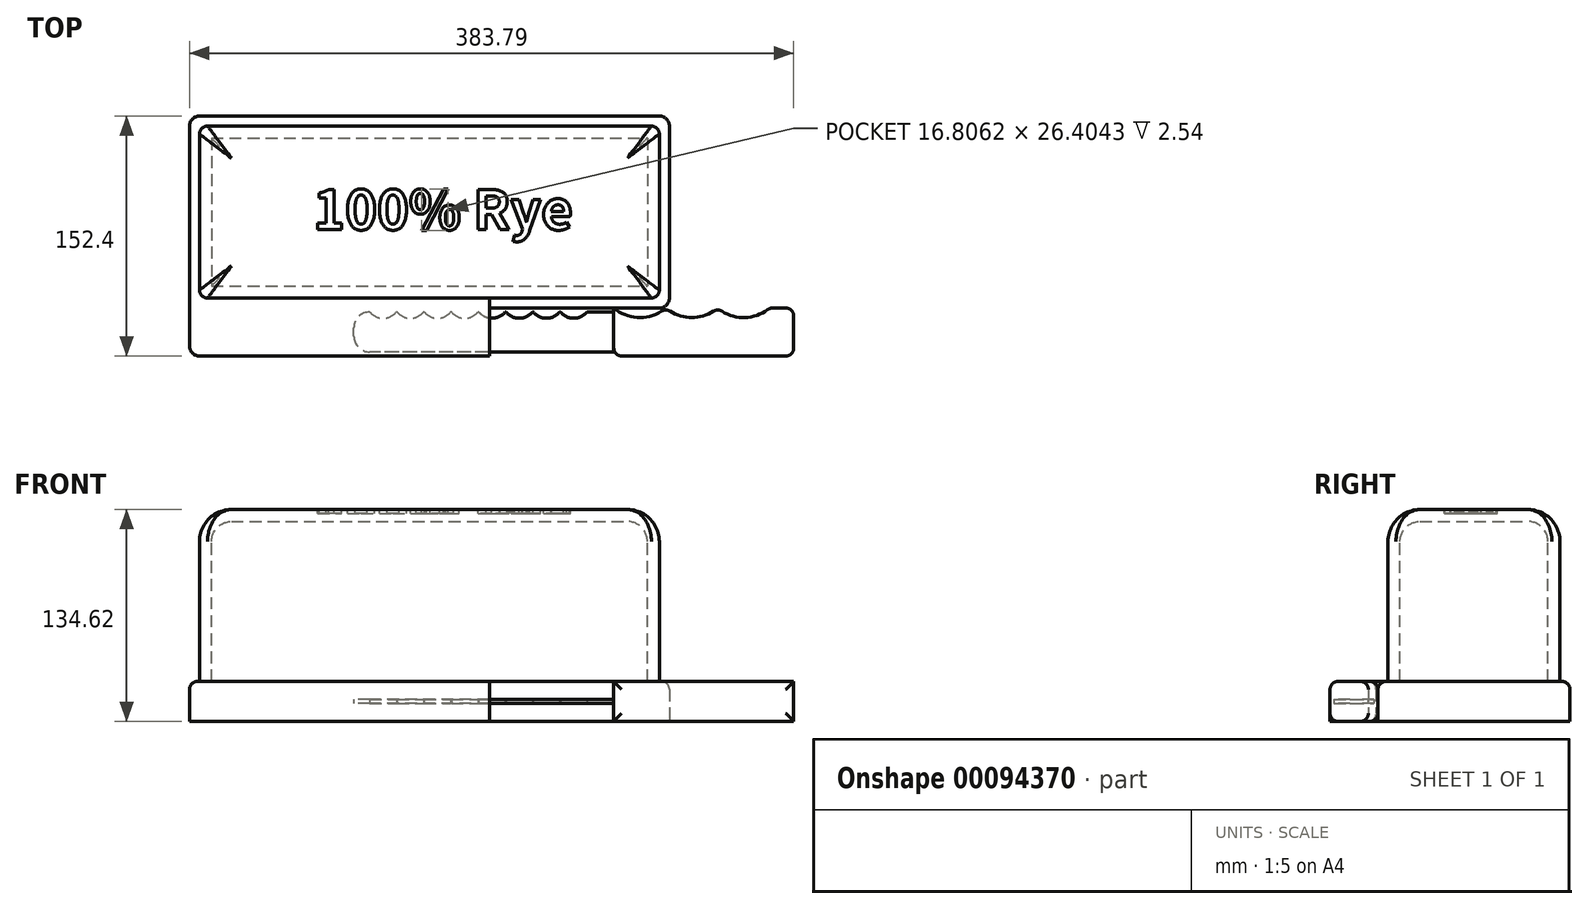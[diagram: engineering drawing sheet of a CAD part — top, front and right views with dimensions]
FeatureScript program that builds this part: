
annotation { "Feature Type Name" : "Feature", "Feature Type Description" : "" }
export const myFeature = defineFeature(function(context is Context, id is Id, definition is map)
    precondition{}
    {
        {
            var Q0;
            Q0=qCreatedBy(makeId("Top.planeOp"),FACE);
            var sketch = newSketch(context, id + "F0", { "sketchPlane" : qUnion([Q0])});
            skLineSegment(sketch, "E0.bottom", {"start": v(-146.05, 76.2) * mm, "end": v(146.05, 76.2) * mm});
            skLineSegment(sketch, "E0.top", {"start": v(-146.05, -76.2) * mm, "end": v(152.4, -76.2) * mm});
            skLineSegment(sketch, "E0.left", {"start": v(-152.4, 69.85) * mm, "end": v(-152.4, -69.85) * mm});
            skLineSegment(sketch, "E0.right", {"start": v(152.4, 69.85) * mm, "end": v(152.4, -45.72) * mm});
            skPoint(sketch, "E0.middle", {"position": v(0, 0) * mm});
            skPoint(sketch, "E1.visualSharp", {"position": v(-152.4, 76.2) * mm});
            skArc(sketch, "E1.filletArc", {"start": v(-146.05, 76.2) * mm, "mid": v(-150.54, 74.34) * mm, "end": v(-152.4, 69.85) * mm});
            skPoint(sketch, "E2.visualSharp", {"position": v(152.4, 76.2) * mm});
            skArc(sketch, "E2.filletArc", {"start": v(152.4, 69.85) * mm, "mid": v(150.54, 74.34) * mm, "end": v(146.05, 76.2) * mm});
            skLineSegment(sketch, "E3.top", {"start": v(152.4, -45.72) * mm, "end": v(38.1, -45.72) * mm});
            skLineSegment(sketch, "E3.left", {"start": v(152.4, -76.2) * mm, "end": v(152.4, -45.72) * mm});
            skLineSegment(sketch, "E3.right", {"start": v(38.1, -76.2) * mm, "end": v(38.1, -45.72) * mm});
            skLineSegment(sketch, "E4", {"start": v(152.4, -45.72) * mm, "end": v(152.4, -76.2) * mm});
            skArc(sketch, "E5", {"start": v(38.1, -45.72) * mm, "mid": v(54.61, -51.82) * mm, "end": v(71.12, -45.72) * mm});
            skArc(sketch, "E6", {"start": v(71.12, -45.72) * mm, "mid": v(87.63, -51.82) * mm, "end": v(104.14, -45.72) * mm});
            skArc(sketch, "E7", {"start": v(104.14, -45.72) * mm, "mid": v(120.65, -51.82) * mm, "end": v(137.16, -45.72) * mm});
            skPoint(sketch, "E8.visualSharp", {"position": v(-152.4, -76.2) * mm});
            skArc(sketch, "E8.filletArc", {"start": v(-152.4, -69.85) * mm, "mid": v(-150.54, -74.34) * mm, "end": v(-146.05, -76.2) * mm});
            skSolve(sketch);
        }
        {
            var Q0;
            {var subQ1=sQuery(id+"F0.wireOp",EDGE,"E3.right");Q0=makeQuery(id+"F0.imprint","IMPRINT",FACE,{"disambiguationData":[TD([[makeQuery(id+"F0.imprint","IMPRINT",EDGE,{"derivedFrom":subQ1}),-1.0]])]});}
            extrude(context, id + "F1", {"entities" : qUnion([Q0]), "depth" : 25.4 * mm});
        }
        {
            var Q0;
            Q0=makeQuery(id+"F1.opExtrude","SWEPT_EDGE",EDGE,{"disambiguationData":[OSD([sQuery(id+"F0.wireOp",EDGE,"E0.right"),sQuery(id+"F0.wireOp",EDGE,"E3.top"),sQuery(id+"F0.wireOp",EDGE,"E4")])]});
            var Q1;
            Q1=makeQuery(id+"F1.opExtrude","SWEPT_EDGE",EDGE,{"disambiguationData":[OSD([sQuery(id+"F0.wireOp",EDGE,"E0.top"),sQuery(id+"F0.wireOp",EDGE,"E4")])]});
            var Q2;
            Q2=makeQuery(id+"F1.opExtrude","SWEPT_EDGE",EDGE,{"disambiguationData":[OSD([sQuery(id+"F0.wireOp",EDGE,"E3.top"),sQuery(id+"F0.wireOp",EDGE,"E7")])]});
            var Q3;
            Q3=makeQuery(id+"F1.opExtrude","SWEPT_EDGE",EDGE,{"disambiguationData":[OSD([sQuery(id+"F0.wireOp",EDGE,"E3.top"),sQuery(id+"F0.wireOp",EDGE,"E6"),sQuery(id+"F0.wireOp",EDGE,"E7")])]});
            var Q4;
            Q4=makeQuery(id+"F1.opExtrude","SWEPT_EDGE",EDGE,{"disambiguationData":[OSD([sQuery(id+"F0.wireOp",EDGE,"E3.top"),sQuery(id+"F0.wireOp",EDGE,"E5"),sQuery(id+"F0.wireOp",EDGE,"E6")])]});
            var Q5;
            Q5=makeQuery(id+"F1.opExtrude","CAP_EDGE",EDGE,{"disambiguationData":[OSD([sQuery(id+"F0.wireOp",EDGE,"E0.top")])],"isStart":false});
            var Q6;
            Q6=makeQuery(id+"F1.opExtrude","CAP_EDGE",EDGE,{"disambiguationData":[OSD([sQuery(id+"F0.wireOp",EDGE,"E0.top")])],"isStart":true});
            var Q7;
            Q7=makeQuery(id+"F1.opExtrude","CAP_EDGE",EDGE,{"disambiguationData":[OSD([sQuery(id+"F0.wireOp",EDGE,"E6")])],"isStart":false});
            var Q8;
            Q8=makeQuery(id+"F1.opExtrude","CAP_EDGE",EDGE,{"disambiguationData":[OSD([sQuery(id+"F0.wireOp",EDGE,"E7")])],"isStart":false});
            var Q9;
            Q9=makeQuery(id+"F1.opExtrude","CAP_EDGE",EDGE,{"disambiguationData":[OSD([sQuery(id+"F0.wireOp",EDGE,"E3.top")])],"isStart":false});
            var Q10;
            Q10=makeQuery(id+"F1.opExtrude","CAP_EDGE",EDGE,{"disambiguationData":[OSD([sQuery(id+"F0.wireOp",EDGE,"E5")])],"isStart":false});
            var Q11;
            Q11=makeQuery(id+"F1.opExtrude","CAP_EDGE",EDGE,{"disambiguationData":[OSD([sQuery(id+"F0.wireOp",EDGE,"E5")])],"isStart":true});
            var Q12;
            Q12=makeQuery(id+"F1.opExtrude","CAP_EDGE",EDGE,{"disambiguationData":[OSD([sQuery(id+"F0.wireOp",EDGE,"E6")])],"isStart":true});
            var Q13;
            Q13=makeQuery(id+"F1.opExtrude","CAP_EDGE",EDGE,{"disambiguationData":[OSD([sQuery(id+"F0.wireOp",EDGE,"E7")])],"isStart":true});
            var Q14;
            Q14=makeQuery(id+"F1.opExtrude","CAP_EDGE",EDGE,{"disambiguationData":[OSD([sQuery(id+"F0.wireOp",EDGE,"E3.top")])],"isStart":true});
            var Q15;
            Q15=makeQuery(id+"F1.opExtrude","CAP_EDGE",EDGE,{"disambiguationData":[OSD([sQuery(id+"F0.wireOp",EDGE,"E4")])],"isStart":false});
            var Q16;
            Q16=makeQuery(id+"F1.opExtrude","CAP_EDGE",EDGE,{"disambiguationData":[OSD([sQuery(id+"F0.wireOp",EDGE,"E4")])],"isStart":true});
            fillet(context, id + "F2", {"entities" : qUnion([Q0, Q1, Q2, Q3, Q4, Q5, Q6, Q7, Q8, Q9, Q10, Q11, Q12, Q13, Q14, Q15, Q16]), "radius" : 5.08 * mm, "tangentPropagation" : true, "allowEdgeOverflow" : false});
        }
        {
            var Q0;
            Q0=makeQuery(id+"F0.imprint","IMPRINT",FACE,{"disambiguationData":[TD([[makeQuery(id+"F0.imprint","IMPRINT",EDGE,{"derivedFrom":sQuery(id+"F0.wireOp",EDGE,"E0.bottom")}),-1.0]])]});
            extrude(context, id + "F3", {"entities" : qUnion([Q0]), "depth" : 25.4 * mm});
        }
        {
            var Q0;
            Q0=makeQuery(id+"F3.opExtrude","SWEPT_EDGE",EDGE,{"disambiguationData":[OSD([sQuery(id+"F0.wireOp",EDGE,"E0.right"),sQuery(id+"F0.wireOp",EDGE,"E3.top"),sQuery(id+"F0.wireOp",EDGE,"E4")])]});
            fillet(context, id + "F4", {"entities" : qUnion([Q0]), "radius" : 6.35 * mm, "tangentPropagation" : true, "allowEdgeOverflow" : false});
        }
        {
            var Q0;
            Q0=makeQuery(id+"F3.opExtrude","CAP_EDGE",EDGE,{"disambiguationData":[OSD([sQuery(id+"F0.wireOp",EDGE,"E0.top")])],"isStart":false});
            fillet(context, id + "F5", {"entities" : qUnion([Q0]), "radius" : 5.08 * mm, "tangentPropagation" : true, "allowEdgeOverflow" : false});
        }
        {
            var Q0;
            Q0=qCreatedBy(makeId("Top.planeOp"),FACE);
            cPlane(context, id + "F6", {"entities" : qUnion([Q0]), "cplaneType" : CPlaneType.OFFSET, "offset" : 12.7 * mm, "width" : 152.4 * mm, "height" : 152.4 * mm});
        }
        {
            var Q0;
            Q0=qCreatedBy(id+"F6.planeOp",FACE);
            var sketch = newSketch(context, id + "F7", { "sketchPlane" : qUnion([Q0])});
            skLineSegment(sketch, "E9.bottom", {"start": v(38.1, -73.66) * mm, "end": v(-116.84, -73.66) * mm});
            skLineSegment(sketch, "E9.top", {"start": v(38.1, -48.26) * mm, "end": v(21.07, -48.26) * mm});
            skLineSegment(sketch, "E9.left", {"start": v(38.1, -73.66) * mm, "end": v(38.1, -48.26) * mm});
            skLineSegment(sketch, "E9.right", {"start": v(-127, -63.5) * mm, "end": v(-127, -58.42) * mm});
            skPoint(sketch, "E10.visualSharp", {"position": v(-127, -48.26) * mm});
            skArc(sketch, "E10.filletArc", {"start": v(-116.84, -48.26) * mm, "mid": v(-124.02, -51.24) * mm, "end": v(-127, -58.42) * mm});
            skPoint(sketch, "E11.visualSharp", {"position": v(-127, -73.66) * mm});
            skArc(sketch, "E11.filletArc", {"start": v(-127, -63.5) * mm, "mid": v(-124.02, -70.68) * mm, "end": v(-116.84, -73.66) * mm});
            skArc(sketch, "E12", {"start": v(-116.84, -48.26) * mm, "mid": v(-108.41, -52.2) * mm, "end": v(-99.99, -48.26) * mm});
            skArc(sketch, "E13.1.0.0", {"start": v(-99.55, -48.26) * mm, "mid": v(-91.12, -52.2) * mm, "end": v(-82.7, -48.26) * mm});
            skArc(sketch, "E13.2.0.0", {"start": v(-82.25, -48.26) * mm, "mid": v(-73.83, -52.2) * mm, "end": v(-65.4, -48.26) * mm});
            skArc(sketch, "E13.3.0.0", {"start": v(-64.96, -48.26) * mm, "mid": v(-56.53, -52.2) * mm, "end": v(-48.1, -48.26) * mm});
            skArc(sketch, "E13.4.0.0", {"start": v(-47.67, -48.26) * mm, "mid": v(-39.24, -52.2) * mm, "end": v(-30.81, -48.26) * mm});
            skArc(sketch, "E13.5.0.0", {"start": v(-30.37, -48.26) * mm, "mid": v(-21.95, -52.2) * mm, "end": v(-13.52, -48.26) * mm});
            skArc(sketch, "E13.6.0.0", {"start": v(-13.08, -48.26) * mm, "mid": v(-4.65, -52.2) * mm, "end": v(3.77, -48.26) * mm});
            skArc(sketch, "E13.7.0.0", {"start": v(4.21, -48.26) * mm, "mid": v(12.64, -52.2) * mm, "end": v(21.07, -48.26) * mm});
            skLineSegment(sketch, "E13.direction1", {"start": v(-99.99, -48.26) * mm, "end": v(-99.55, -48.26) * mm, "construction": true});
            skLineSegment(sketch, "E14.trimOffspring", {"start": v(4.21, -48.26) * mm, "end": v(3.77, -48.26) * mm});
            skLineSegment(sketch, "E15.trimOffspring", {"start": v(-13.08, -48.26) * mm, "end": v(-13.52, -48.26) * mm});
            skLineSegment(sketch, "E16.trimOffspring", {"start": v(-30.37, -48.26) * mm, "end": v(-30.81, -48.26) * mm});
            skLineSegment(sketch, "E17.trimOffspring", {"start": v(-47.67, -48.26) * mm, "end": v(-48.1, -48.26) * mm});
            skLineSegment(sketch, "E18.trimOffspring", {"start": v(-64.96, -48.26) * mm, "end": v(-65.4, -48.26) * mm});
            skLineSegment(sketch, "E19.trimOffspring", {"start": v(-82.25, -48.26) * mm, "end": v(-82.7, -48.26) * mm});
            skLineSegment(sketch, "E20.trimOffspring", {"start": v(-99.55, -48.26) * mm, "end": v(-99.99, -48.26) * mm});
            skSolve(sketch);
        }
        {
            var Q0;
            Q0=makeQuery(id+"F7.imprint","IMPRINT",FACE,{"disambiguationData":[TD([[makeQuery(id+"F7.imprint","IMPRINT",EDGE,{"derivedFrom":sQuery(id+"F7.wireOp",EDGE,"E9.bottom")}),-1.0]])]});
            extrude(context, id + "F8", {"entities" : qUnion([Q0]), "endBound" : BoundingType.SYMMETRIC, "depth" : 2.54 * mm});
        }
        {
            var Q0;
            Q0=makeQuery(id+"F3.opExtrude","CAP_FACE",FACE,{"disambiguationData":[OSD([sQuery(id+"F0.wireOp",EDGE,"E0.bottom"),sQuery(id+"F0.wireOp",EDGE,"E0.top"),sQuery(id+"F0.wireOp",EDGE,"E0.left"),sQuery(id+"F0.wireOp",EDGE,"E0.right"),sQuery(id+"F0.wireOp",EDGE,"E1.filletArc"),sQuery(id+"F0.wireOp",EDGE,"E2.filletArc"),sQuery(id+"F0.wireOp",EDGE,"E3.top"),sQuery(id+"F0.wireOp",EDGE,"E3.right"),sQuery(id+"F0.wireOp",EDGE,"E8.filletArc")])],"isStart":false});
            var sketch = newSketch(context, id + "F9", { "sketchPlane" : qUnion([Q0])});
            skLineSegment(sketch, "E21.bottom", {"start": v(-146.05, 69.85) * mm, "end": v(146.05, 69.85) * mm});
            skLineSegment(sketch, "E21.top", {"start": v(-146.05, -39.37) * mm, "end": v(146.05, -39.37) * mm});
            skLineSegment(sketch, "E21.left", {"start": v(-146.05, 69.85) * mm, "end": v(-146.05, -39.37) * mm});
            skLineSegment(sketch, "E21.right", {"start": v(146.05, 69.85) * mm, "end": v(146.05, -39.37) * mm});
            skSolve(sketch);
        }
        {
            var Q0;
            Q0=makeQuery(id+"F9.imprint","IMPRINT",FACE,{"disambiguationData":[TD([[makeQuery(id+"F9.imprint","IMPRINT",EDGE,{"derivedFrom":sQuery(id+"F9.wireOp",EDGE,"E21.bottom")}),-1.0]])]});
            extrude(context, id + "F10", {"entities" : qUnion([Q0]), "depth" : 109.22 * mm});
        }
        {
            var Q0;
            Q0=makeQuery(id+"F10.opExtrude","SWEPT_EDGE",EDGE,{"disambiguationData":[OSD([sQuery(id+"F9.wireOp",EDGE,"E21.top"),sQuery(id+"F9.wireOp",EDGE,"E21.left")])]});
            var Q1;
            Q1=makeQuery(id+"F10.opExtrude","SWEPT_EDGE",EDGE,{"disambiguationData":[OSD([sQuery(id+"F9.wireOp",EDGE,"E21.bottom"),sQuery(id+"F9.wireOp",EDGE,"E21.left")])]});
            var Q2;
            Q2=makeQuery(id+"F10.opExtrude","SWEPT_EDGE",EDGE,{"disambiguationData":[OSD([sQuery(id+"F9.wireOp",EDGE,"E21.bottom"),sQuery(id+"F9.wireOp",EDGE,"E21.right")])]});
            var Q3;
            Q3=makeQuery(id+"F10.opExtrude","SWEPT_EDGE",EDGE,{"disambiguationData":[OSD([sQuery(id+"F9.wireOp",EDGE,"E21.top"),sQuery(id+"F9.wireOp",EDGE,"E21.right")])]});
            fillet(context, id + "F11", {"entities" : qUnion([Q0, Q1, Q2, Q3]), "radius" : 5.08 * mm, "tangentPropagation" : true, "allowEdgeOverflow" : false});
        }
        {
            var Q0;
            Q0=makeQuery(id+"F10.opExtrude","CAP_EDGE",EDGE,{"disambiguationData":[OSD([sQuery(id+"F9.wireOp",EDGE,"E21.top")])],"isStart":false});
            fillet(context, id + "F12", {"entities" : qUnion([Q0]), "radius" : 20.32 * mm, "tangentPropagation" : true, "allowEdgeOverflow" : false});
        }
        {
            var Q0;
            Q0=makeQuery(id+"F10.opExtrude","CAP_FACE",FACE,{"disambiguationData":[OSD([sQuery(id+"F9.wireOp",EDGE,"E21.bottom"),sQuery(id+"F9.wireOp",EDGE,"E21.top"),sQuery(id+"F9.wireOp",EDGE,"E21.left"),sQuery(id+"F9.wireOp",EDGE,"E21.right")])],"isStart":true});
            shell(context, id + "F13", {"entities" : qUnion([Q0]), "thickness" : 7.62 * mm});
        }
        {
            var Q0;
            Q0=makeQuery(id+"F10.opExtrude","CAP_FACE",FACE,{"disambiguationData":[OSD([sQuery(id+"F9.wireOp",EDGE,"E21.bottom"),sQuery(id+"F9.wireOp",EDGE,"E21.top"),sQuery(id+"F9.wireOp",EDGE,"E21.left"),sQuery(id+"F9.wireOp",EDGE,"E21.right")])],"isStart":false});
            var sketch = newSketch(context, id + "F14", { "sketchPlane" : qUnion([Q0])});
            skText(sketch, "E22", { "text": "100% Rye", "fontName": "NotoSansCJKsc-Bold.otf"});
            const initialGuessF14  = {"E22": [-0.07377, 0.00404, 1, 0, 0.02475]};
            skSetInitialGuess(sketch, initialGuessF14);
            skSolve(sketch);
        }
        {
            var Q0;
            Q0 = qSketchRegion(id + "F14", true);
            extrude(context, id + "F15", {"entities" : qUnion([Q0]), "operationType" : NewBodyOperationType.REMOVE, "oppositeDirection" : true, "depth" : 2.54 * mm});
        }
        {
            var Q0;
            Q0=makeQuery(id+"F1.opExtrude","SWEPT_BODY",BODY,{"disambiguationData":[OSD([sQuery(id+"F0.wireOp",EDGE,"E0.top"),sQuery(id+"F0.wireOp",EDGE,"E3.top"),sQuery(id+"F0.wireOp",EDGE,"E3.right"),sQuery(id+"F0.wireOp",EDGE,"E4"),sQuery(id+"F0.wireOp",EDGE,"E5"),sQuery(id+"F0.wireOp",EDGE,"E6"),sQuery(id+"F0.wireOp",EDGE,"E7")])]});
            var Q1;
            Q1=makeQuery(id+"F8.opExtrude","SWEPT_BODY",BODY,{"disambiguationData":[OSD([sQuery(id+"F7.wireOp",EDGE,"E9.bottom"),sQuery(id+"F7.wireOp",EDGE,"E9.top"),sQuery(id+"F7.wireOp",EDGE,"E9.left"),sQuery(id+"F7.wireOp",EDGE,"E9.right"),sQuery(id+"F7.wireOp",EDGE,"E10.filletArc"),sQuery(id+"F7.wireOp",EDGE,"E11.filletArc"),sQuery(id+"F7.wireOp",EDGE,"E12"),sQuery(id+"F7.wireOp",EDGE,"E13.1.0.0"),sQuery(id+"F7.wireOp",EDGE,"E13.2.0.0"),sQuery(id+"F7.wireOp",EDGE,"E13.3.0.0"),sQuery(id+"F7.wireOp",EDGE,"E13.4.0.0"),sQuery(id+"F7.wireOp",EDGE,"E13.5.0.0"),sQuery(id+"F7.wireOp",EDGE,"E13.6.0.0"),sQuery(id+"F7.wireOp",EDGE,"E13.7.0.0"),sQuery(id+"F7.wireOp",EDGE,"E14.trimOffspring"),sQuery(id+"F7.wireOp",EDGE,"E15.trimOffspring"),sQuery(id+"F7.wireOp",EDGE,"E16.trimOffspring"),sQuery(id+"F7.wireOp",EDGE,"E17.trimOffspring"),sQuery(id+"F7.wireOp",EDGE,"E18.trimOffspring"),sQuery(id+"F7.wireOp",EDGE,"E19.trimOffspring"),sQuery(id+"F7.wireOp",EDGE,"E20.trimOffspring")])]});
            transform(context, id + "F16", {"entities" : qUnion([Q0, Q1]), "transformType" : TransformType.TRANSLATION_3D, "dx" : 78.99 * mm, "dy" : 0 * mm, "dz" : 0 * mm, "makeCopy" : false});
        }
    });
